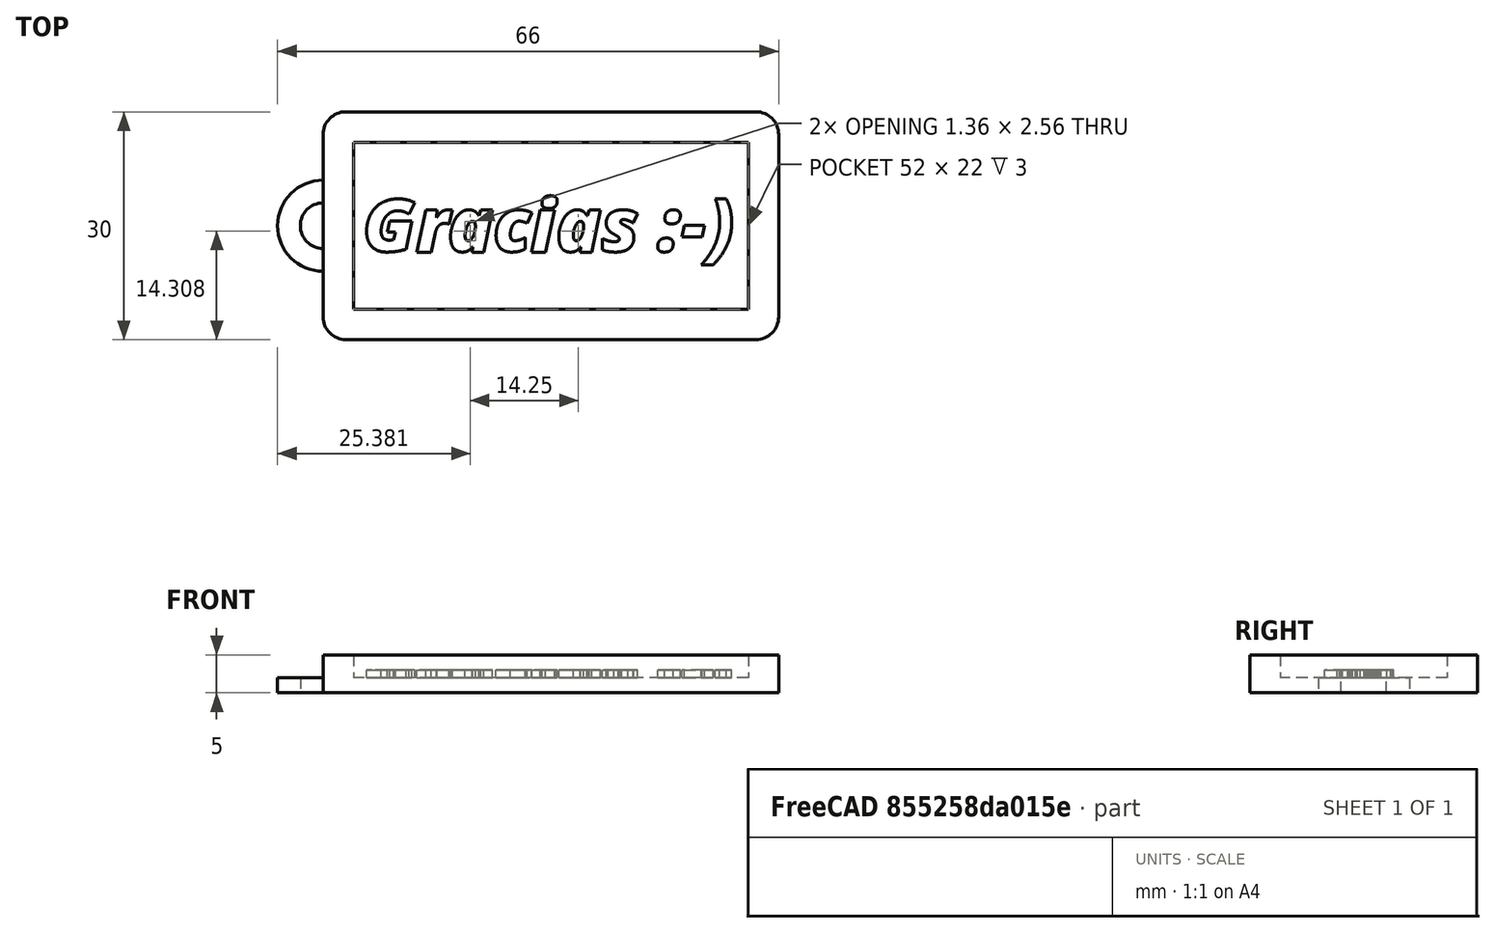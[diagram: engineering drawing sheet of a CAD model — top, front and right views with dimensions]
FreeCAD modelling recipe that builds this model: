
FCSTD DOCUMENT  (FreeCAD 0.17R13217 (Git))
Label: 10-llavero-nombre
License: All rights reserved
LicenseURL: http://en.wikipedia.org/wiki/All_rights_reserved
objects: TechDraw::DrawViewDimension×8, Sketcher::SketchObject×3, PartDesign::Pad×2, TechDraw::DrawProjGroupItem×2, PartDesign::Plane×1, PartDesign::Pocket×1, Part::Part2DObjectPython×1, Part::Extrusion×1, PartDesign::Fillet×1, PartDesign::Body×1, App::Part×1, TechDraw::DrawSVGTemplate×1, TechDraw::DrawProjGroup×1, TechDraw::DrawViewPart×1, TechDraw::DrawViewAnnotation×1, TechDraw::DrawPage×1
note: 14 computed .brp shape members not serialized (recipe doc carries the construction recipe); baked Part::Feature solids carry a one-line shape summary decoded from their .brp

FEATURE [Sketcher::SketchObject] Sketch
  MapMode = 5
  Support = -> [XY_Plane]
  sketch-geometry (4):
    g0: LineSegment StartX=-30 StartY=15 StartZ=0 EndX=30 EndY=15 EndZ=0
    g1: LineSegment StartX=30 StartY=15 StartZ=0 EndX=30 EndY=-15 EndZ=0
    g2: LineSegment StartX=30 StartY=-15 StartZ=0 EndX=-30 EndY=-15 EndZ=0
    g3: LineSegment StartX=-30 StartY=-15 StartZ=0 EndX=-30 EndY=15 EndZ=0
  constraints (11):
    c: Coincident(g0,g1)
    c: Coincident(g1,g2)
    c: Coincident(g2,g3)
    c: Coincident(g3,g0)
    c: Horizontal(g0)
    c: Horizontal(g2)
    c: Vertical(g1)
    c: Vertical(g3)
    c: Symmetric(g0,g1,g-1)
    c: DistanceX(g0,g0) = 60
    c: DistanceY(g1,g1) = 30
FEATURE [PartDesign::Pad] Pad
  Length = 5
  Length2 = 100
  Profile = -> Sketch
  Refine = true
  Type = 0
FEATURE [PartDesign::Plane] DatumPlane
  MapMode = 5
  Placement = pos=(0,0,5) rot=(0,0,1;0rad)
  Support = -> [Pad]
FEATURE [Sketcher::SketchObject] Sketch001
  ExternalGeometry = -> [Pad]
  MapMode = 5
  Placement = pos=(0,0,5) rot=(0,0,1;0rad)
  Support = -> [DatumPlane]
  sketch-geometry (5):
    g0: LineSegment StartX=-26 StartY=11 StartZ=0 EndX=26 EndY=11 EndZ=0
    g1: LineSegment StartX=26 StartY=11 StartZ=0 EndX=26 EndY=-11 EndZ=0
    g2: LineSegment StartX=26 StartY=-11 StartZ=0 EndX=-26 EndY=-11 EndZ=0
    g3: LineSegment StartX=-26 StartY=-11 StartZ=0 EndX=-26 EndY=11 EndZ=0
    g4: LineSegment [constr] StartX=-30 StartY=15 StartZ=0 EndX=-26 EndY=11 EndZ=0
  constraints (13):
    c: Coincident(g0,g1)
    c: Coincident(g1,g2)
    c: Coincident(g2,g3)
    c: Coincident(g3,g0)
    c: Horizontal(g0)
    c: Horizontal(g2)
    c: Vertical(g1)
    c: Vertical(g3)
    c: Symmetric(g0,g1,g-1)
    c: Coincident(g4,g-3)
    c: Coincident(g4,g0)
    c: Angle(g4,g-3) = 0.785398
    c: DistanceX(g4,g0) = 4
FEATURE [PartDesign::Pocket] Pocket
  BaseFeature = -> Pad
  Length = 3
  Length2 = 100
  Profile = -> Sketch001
  Refine = true
  Type = 0
FEATURE [Part::Part2DObjectPython] ShapeString  label="Texto"  # Draft 2D object (typed FeaturePython)
  FontFile = <userpath>/develop/CTIF-Madrid-2018-FreeCAD/Sesion-6/OpenSans/OpenSans-ExtraBoldItalic.ttf
  Placement = pos=(-24.7708,-3.48014,2) rot=(0,0,1;0rad)
  Size = 9
  String = Gracias :-)
  Tracking = 0
FEATURE [Part::Extrusion] Extrude  label="Nombre"
  Base = -> ShapeString
  Dir = (0,0,1)
  DirMode = 2
  FaceMakerClass = Part::FaceMakerBullseye
  LengthFwd = 1
  LengthRev = 0
  Solid = false
  Symmetric = false
FEATURE [PartDesign::Fillet] Fillet
  Base = -> Pocket [Edge5,Edge8,Edge2,Edge1]
  BaseFeature = -> Pocket
  Radius = 3
FEATURE [Sketcher::SketchObject] Sketch002
  ExternalGeometry = -> [Fillet]
  MapMode = 5
  Support = -> [XY_Plane]
  sketch-geometry (3):
    g0: Circle CenterX=-30 CenterY=0 CenterZ=0 NormalX=0 NormalY=0 NormalZ=1 AngleXU=0 Radius=6
    g1: ArcOfCircle CenterX=-30 CenterY=0 CenterZ=0 NormalX=0 NormalY=0 NormalZ=1 AngleXU=0 Radius=3 StartAngle=1.5708 EndAngle=4.71239
    g2: LineSegment StartX=-30 StartY=3 StartZ=0 EndX=-30 EndY=-3 EndZ=0
  constraints (9):
    c: PointOnObject(g0,g-1)
    c: PointOnObject(g0,g-3)
    c: Coincident(g1,g0)
    c: PointOnObject(g1,g-3)
    c: PointOnObject(g1,g-3)
    c: Coincident(g2,g1)
    c: Coincident(g2,g1)
    c: Radius(g1) = 3
    c: Radius(g0) = 6
FEATURE [PartDesign::Pad] Pad001
  BaseFeature = -> Fillet
  Length = 10
  Length2 = 100
  Profile = -> Sketch002
  Refine = true
  Type = 3
  UpToFace = -> Fillet [Face15]
FEATURE [PartDesign::Body] Body  label="llavero-sin-texto"
  Group = -> [Sketch,Pad,DatumPlane,Sketch001,Pocket,Fillet,Sketch002,Pad001]
  Origin = -> Origin
  Tip = -> Pad001
FEATURE [App::Part] Part  label="Llavero"
  Group = -> [Body,ShapeString,Extrude]
  License = CC BY 3.0
  LicenseURL = http://creativecommons.org/licenses/by/3.0/
  Origin = -> Origin002
FEATURE [TechDraw::DrawSVGTemplate] Template
  EditableTexts = Designed_by_Name=Designed by Name; Drawing_number=Drawing number; FC-Date=Date; FC-SC=Scale; FC-SH=Sheet; FC-Title=Title; Subtitle=Subtitle; Weight=Weight
  Height = 210
  Orientation = 1
  Width = 297
FEATURE [TechDraw::DrawProjGroupItem] ProjItem  label="Front"
  ArcCenterMarks = true
  CenterScale = 2
  CoarseView = false
  Direction = (0,-1,0)
  ExtraWidth = 1.4
  Focus = 100
  HardHidden = true
  HiddenWidth = 0.35
  HorizCenterLine = false
  IsoCount = 0
  IsoHidden = false
  IsoVisible = false
  IsoWidth = 0.5
  KeepLabel = false
  LineWidth = 0.7
  LockPosition = false
  Perspective = false
  Rotation = 0
  RotationVector = (1,0,0)
  ScaleType = 0
  SeamHidden = false
  SeamVisible = false
  ShowSectionLine = true
  SmoothHidden = false
  SmoothVisible = false
  Source = -> [Part]
  Type = 0
  VertCenterLine = false
  X = 0
  Y = 0
FEATURE [TechDraw::DrawProjGroupItem] ProjItem001  label="Top"
  ArcCenterMarks = true
  CenterScale = 2
  CoarseView = false
  Direction = (0,0,1)
  ExtraWidth = 1.4
  Focus = 100
  HardHidden = false
  HiddenWidth = 0.35
  HorizCenterLine = false
  IsoCount = 0
  IsoHidden = false
  IsoVisible = false
  IsoWidth = 0.5
  KeepLabel = false
  LineWidth = 0.7
  LockPosition = false
  Perspective = false
  Rotation = 0
  RotationVector = (1,0,0)
  ScaleType = 0
  SeamHidden = false
  SeamVisible = false
  ShowSectionLine = true
  SmoothHidden = false
  SmoothVisible = false
  Source = -> [Part]
  Type = 4
  VertCenterLine = false
  X = 0
  Y = -45
FEATURE [TechDraw::DrawProjGroup] ProjGroup
  Anchor = -> ProjItem
  AutoDistribute = true
  CubeDirs = (1) [(0,0,0)]
  CubeRotations = (1) [(0,0,0)]
  KeepLabel = false
  LockPosition = false
  ProjectionType = 0
  Rotation = 0
  ScaleType = 0
  Source = -> [Part]
  Views = -> [ProjItem,ProjItem001]
  X = 76.7028
  Y = 167.711
  spacingX = 15
  spacingY = 15
FEATURE [TechDraw::DrawViewPart] View
  ArcCenterMarks = true
  CenterScale = 2
  CoarseView = false
  Direction = (1,-1,1)
  ExtraWidth = 1.4
  Focus = 100
  HardHidden = false
  HiddenWidth = 0.35
  HorizCenterLine = false
  IsoCount = 0
  IsoHidden = false
  IsoVisible = false
  IsoWidth = 0.5
  KeepLabel = false
  LineWidth = 0.7
  LockPosition = false
  Perspective = false
  Rotation = 0
  Scale = 2
  ScaleType = 0
  SeamHidden = false
  SeamVisible = false
  ShowSectionLine = true
  SmoothHidden = false
  SmoothVisible = false
  Source = -> [Part]
  VertCenterLine = false
  X = 210.513
  Y = 129.84
FEATURE [TechDraw::DrawViewDimension] Dimension
  Font = osifont
  Fontsize = 3.5
  FormatSpec = %.2f
  KeepLabel = false
  LineWidth = 0.5
  LockPosition = false
  MeasureType = 1
  References2D = -> [ProjItem001]
  Rotation = 0
  ScaleType = 0
  Type = 1
  X = 0.232044
  Y = 36.1989
FEATURE [TechDraw::DrawViewDimension] Dimension001
  Font = osifont
  Fontsize = 3.5
  FormatSpec = %.2f
  KeepLabel = false
  LineWidth = 0.5
  LockPosition = false
  MeasureType = 1
  References2D = -> [ProjItem001]
  Rotation = 0
  ScaleType = 0
  Type = 2
  X = 45.2486
  Y = -0.464088
FEATURE [TechDraw::DrawViewDimension] Dimension002
  Font = osifont
  Fontsize = 3.5
  FormatSpec = %.2f
  KeepLabel = false
  LineWidth = 0.5
  LockPosition = false
  MeasureType = 1
  References2D = -> [ProjItem001]
  Rotation = 0
  ScaleType = 0
  Type = 4
  X = -46.8729
  Y = -21.8122
FEATURE [TechDraw::DrawViewDimension] Dimension003
  Font = osifont
  Fontsize = 3.5
  FormatSpec = %.2f
  KeepLabel = false
  LineWidth = 0.5
  LockPosition = false
  MeasureType = 1
  References2D = -> [ProjItem]
  Rotation = 0
  ScaleType = 0
  Type = 2
  X = 42.6961
  Y = -15.3149
FEATURE [TechDraw::DrawViewDimension] Dimension004
  Font = osifont
  Fontsize = 3.5
  FormatSpec = %.2f
  KeepLabel = false
  LineWidth = 0.5
  LockPosition = false
  MeasureType = 1
  References2D = -> [ProjItem001]
  Rotation = 0
  ScaleType = 0
  Type = 1
  X = 14.6188
  Y = -24.5967
FEATURE [TechDraw::DrawViewDimension] Dimension005
  Font = osifont
  Fontsize = 3.5
  FormatSpec = %.2f
  KeepLabel = false
  LineWidth = 0.5
  LockPosition = false
  MeasureType = 1
  References2D = -> [ProjItem001]
  Rotation = 0
  ScaleType = 0
  Type = 4
  X = -51.0502
  Y = 13.1332
FEATURE [TechDraw::DrawViewDimension] Dimension006
  Font = osifont
  Fontsize = 3.5
  FormatSpec = %.2f
  KeepLabel = false
  LineWidth = 0.5
  LockPosition = false
  MeasureType = 1
  References2D = -> [ProjItem001]
  Rotation = 0
  ScaleType = 0
  Type = 4
  X = -54.863
  Y = -10.8031
FEATURE [TechDraw::DrawViewDimension] Dimension007
  Font = osifont
  Fontsize = 3.5
  FormatSpec = %.2f
  KeepLabel = false
  LineWidth = 0.5
  LockPosition = false
  MeasureType = 1
  References2D = -> [ProjItem]
  Rotation = 0
  ScaleType = 0
  Type = 2
  X = 53.5921
  Y = 8.47306
FEATURE [TechDraw::DrawViewAnnotation] Annotation
  Font = osifont
  KeepLabel = false
  LineSpace = 80
  LockPosition = false
  MaxWidth = -1
  Rotation = 0
  ScaleType = 0
  Text = Llavero
  TextSize = 8
  TextStyle = 1
  X = 81.6713
  Y = 57.663
FEATURE [TechDraw::DrawPage] Page
  KeepUpdated = true
  ProjectionType = 0
  Template = -> Template
  Views = -> [ProjGroup,View,Dimension,Dimension001,Dimension002,Dimension003,Dimension004,Dimension005,Dimension006,Dimension007,Annotation]
